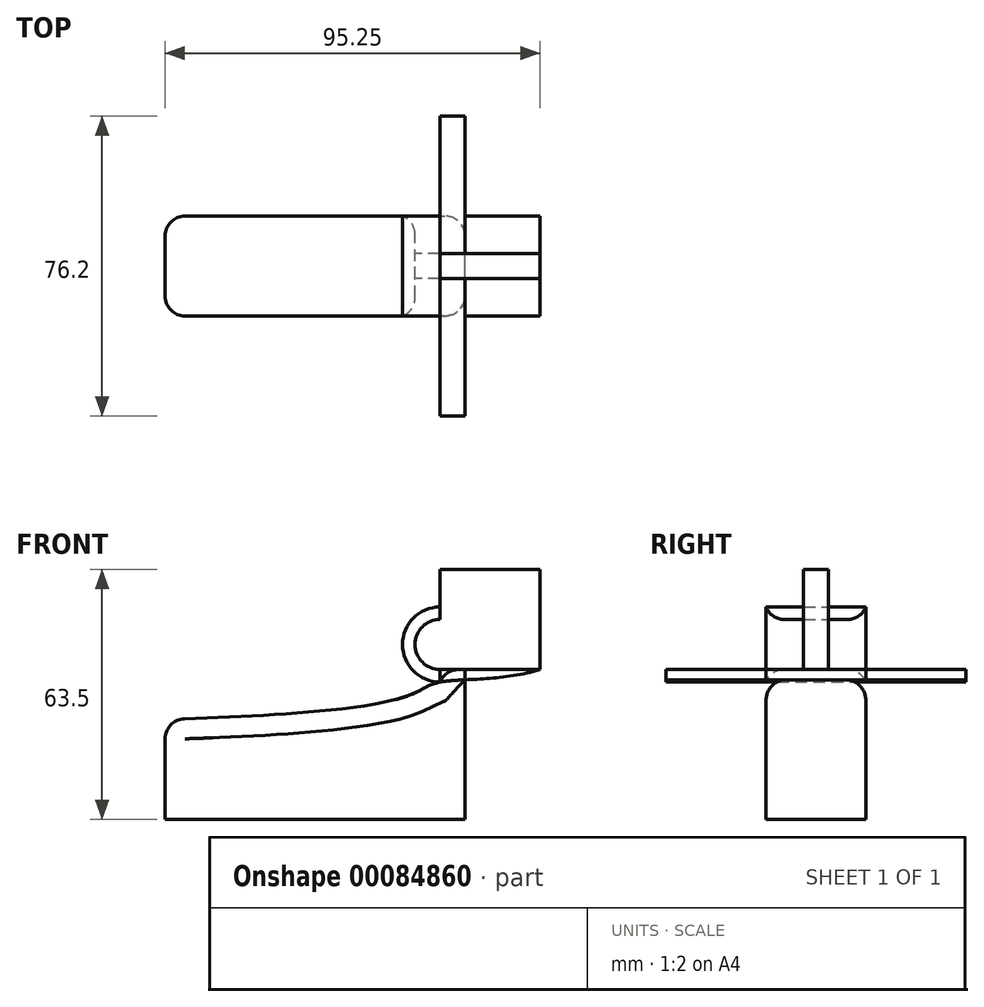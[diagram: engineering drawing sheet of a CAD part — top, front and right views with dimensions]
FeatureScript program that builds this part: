
annotation { "Feature Type Name" : "Feature", "Feature Type Description" : "" }
export const myFeature = defineFeature(function(context is Context, id is Id, definition is map)
    precondition{}
    {
        {
            var Q0;
            Q0=qCreatedBy(makeId("Front.planeOp"),FACE);
            var sketch = newSketch(context, id + "F0", { "sketchPlane" : qUnion([Q0])});
            skLineSegment(sketch, "E0.bottom", {"start": v(-38.1, -12.7) * mm, "end": v(38.1, -12.7) * mm});
            skLineSegment(sketch, "E0.top", {"start": v(-38.1, 12.7) * mm, "end": v(38.1, 12.7) * mm});
            skLineSegment(sketch, "E0.left", {"start": v(-38.1, -12.7) * mm, "end": v(-38.1, 12.7) * mm});
            skLineSegment(sketch, "E0.right", {"start": v(38.1, -12.7) * mm, "end": v(38.1, 12.7) * mm});
            skPoint(sketch, "E0.middle", {"position": v(0, 0) * mm});
            skLineSegment(sketch, "E1.bottom", {"start": v(31.75, 25.4) * mm, "end": v(57.15, 25.4) * mm});
            skLineSegment(sketch, "E1.top", {"start": v(31.75, 50.8) * mm, "end": v(57.15, 50.8) * mm});
            skLineSegment(sketch, "E1.left", {"start": v(31.75, 38.1) * mm, "end": v(31.75, 50.8) * mm});
            skLineSegment(sketch, "E1.right", {"start": v(57.15, 25.4) * mm, "end": v(57.15, 50.8) * mm});
            skPoint(sketch, "E1.middle", {"position": v(44.45, 38.1) * mm});
            skLineSegment(sketch, "E2", {"start": v(38.1, 12.7) * mm, "end": v(38.1, 25.4) * mm});
            skArc(sketch, "E3", {"start": v(31.75, 38.1) * mm, "mid": v(25.4, 31.75) * mm, "end": v(31.75, 25.4) * mm});
            skArc(sketch, "E4.0", {"start": v(31.75, 41.27) * mm, "mid": v(22.22, 31.75) * mm, "end": v(31.75, 22.23) * mm});
            skLineSegment(sketch, "E5", {"start": v(31.75, 22.23) * mm, "end": v(31.75, 25.4) * mm});
            skLineSegment(sketch, "E6", {"start": v(31.75, 41.27) * mm, "end": v(31.75, 38.1) * mm});
            skFitSpline(sketch, "E7", {"points": [v(-38.1, 12.7) * mm, v(31.75, 22.23) * mm, v(57.15, 25.4) * mm], "startDerivative": vector(339.49, 10.11) * mm, "endDerivative": vector(73.4, 23.68) * mm});
            skSolve(sketch);
        }
        {
            var Q0;
            Q0=makeQuery(id+"F0.imprint","IMPRINT",FACE,{"disambiguationData":[TD([[makeQuery(id+"F0.imprint","IMPRINT",EDGE,{"derivedFrom":sQuery(id+"F0.wireOp",EDGE,"E0.bottom")}),1.0]])]});
            var Q1;
            Q1=makeQuery(id+"F0.imprint","IMPRINT",FACE,{"disambiguationData":[TD([[makeQuery(id+"F0.imprint","IMPRINT",EDGE,{"derivedFrom":sQuery(id+"F0.wireOp",EDGE,"E3")}),-1.0]])]});
            var Q2;
            {var subQ1=sQuery(id+"F0.wireOp",EDGE,"E1.bottom");var subQ3=sQuery(id+"F0.wireOp",EDGE,"E2");var subQ4=makeQuery(id+"F0.imprint","INTERSECT",VERTEX,{"derivedFrom":[subQ1,subQ3]});Q2=makeQuery(id+"F0.imprint","IMPRINT",FACE,{"disambiguationData":[TD([[makeQuery(id+"F0.imprint","IMPRINT",EDGE,{"disambiguationData":[TD([[subQ4,1.0]])],"derivedFrom":subQ3}),-1.0]])]});}
            var Q3;
            {var subQ0=sQuery(id+"F0.wireOp",EDGE,"E0.top");Q3=makeQuery(id+"F0.imprint","IMPRINT",FACE,{"disambiguationData":[TD([[makeQuery(id+"F0.imprint","IMPRINT",EDGE,{"derivedFrom":subQ0}),1.0]])]});}
            extrude(context, id + "F1", {"entities" : qUnion([Q0, Q1, Q2, Q3]), "endBound" : BoundingType.SYMMETRIC, "depth" : 25.4 * mm});
        }
        {
            var Q0;
            {var subQ0=sQuery(id+"F0.wireOp",EDGE,"E5");Q0=makeQuery(id+"F0.imprint","IMPRINT",FACE,{"disambiguationData":[TD([[makeQuery(id+"F0.imprint","IMPRINT",EDGE,{"derivedFrom":subQ0}),-1.0]])]});}
            extrude(context, id + "F2", {"entities" : qUnion([Q0]), "endBound" : BoundingType.SYMMETRIC, "depth" : 76.2 * mm});
        }
        {
            var Q0;
            Q0=makeQuery(id+"F0.imprint","IMPRINT",FACE,{"disambiguationData":[TD([[makeQuery(id+"F0.imprint","IMPRINT",EDGE,{"derivedFrom":sQuery(id+"F0.wireOp",EDGE,"E1.top")}),-1.0]])]});
            extrude(context, id + "F3", {"entities" : qUnion([Q0]), "endBound" : BoundingType.SYMMETRIC, "depth" : 6.35 * mm});
        }
        {
            var Q0;
            {var subQ0=sQuery(id+"F0.wireOp",EDGE,"E7");Q0=makeQuery(id+"F1.opExtrude","CAP_EDGE",EDGE,{"disambiguationData":[OSD([subQ0]),TDD([makeQuery(id+"F0.imprint","IMPRINT",EDGE,{"disambiguationData":[TD([[makeQuery(id+"F0.imprint","INTERSECT",VERTEX,{"derivedFrom":[sQuery(id+"F0.wireOp",EDGE,"E0.top"),sQuery(id+"F0.wireOp",EDGE,"E0.left"),subQ0]}),-1.0]])],"derivedFrom":subQ0}),makeQuery(id+"F0.imprint","IMPRINT",EDGE,{"disambiguationData":[TD([[makeQuery(id+"F0.imprint","INTERSECT",VERTEX,{"derivedFrom":[sQuery(id+"F0.wireOp",EDGE,"E2"),subQ0]}),1.0]])],"derivedFrom":subQ0})])],"isStart":false});}
            var Q1;
            {var subQ0=sQuery(id+"F0.wireOp",EDGE,"E7");Q1=makeQuery(id+"F1.opExtrude","CAP_EDGE",EDGE,{"disambiguationData":[OSD([subQ0]),TDD([makeQuery(id+"F0.imprint","IMPRINT",EDGE,{"disambiguationData":[TD([[makeQuery(id+"F0.imprint","INTERSECT",VERTEX,{"derivedFrom":[sQuery(id+"F0.wireOp",EDGE,"E0.top"),sQuery(id+"F0.wireOp",EDGE,"E0.left"),subQ0]}),-1.0]])],"derivedFrom":subQ0}),makeQuery(id+"F0.imprint","IMPRINT",EDGE,{"disambiguationData":[TD([[makeQuery(id+"F0.imprint","INTERSECT",VERTEX,{"derivedFrom":[sQuery(id+"F0.wireOp",EDGE,"E2"),subQ0]}),1.0]])],"derivedFrom":subQ0})])],"isStart":true});}
            var Q2;
            Q2=makeQuery(id+"F1.opExtrude","CAP_EDGE",EDGE,{"disambiguationData":[OSD([sQuery(id+"F0.wireOp",EDGE,"E0.right"),sQuery(id+"F0.wireOp",EDGE,"E2")])],"isStart":false});
            var Q3;
            Q3=makeQuery(id+"F1.opExtrude","SWEPT_EDGE",EDGE,{"disambiguationData":[OSD([sQuery(id+"F0.wireOp",EDGE,"E0.top"),sQuery(id+"F0.wireOp",EDGE,"E0.left"),sQuery(id+"F0.wireOp",EDGE,"E7")])]});
            var Q4;
            Q4=makeQuery(id+"F1.opExtrude","CAP_EDGE",EDGE,{"disambiguationData":[OSD([sQuery(id+"F0.wireOp",EDGE,"E0.left")])],"isStart":true});
            var Q5;
            Q5=makeQuery(id+"F2.opExtrude","SWEPT_EDGE",EDGE,{"disambiguationData":[OSD([sQuery(id+"F0.wireOp",EDGE,"E1.bottom"),sQuery(id+"F0.wireOp",EDGE,"E3"),sQuery(id+"F0.wireOp",EDGE,"E5")])]});
            var Q6;
            Q6=makeQuery(id+"F1.opExtrude","CAP_EDGE",EDGE,{"disambiguationData":[OSD([sQuery(id+"F0.wireOp",EDGE,"E0.left")])],"isStart":false});
            var Q7;
            Q7=makeQuery(id+"F1.opExtrude","CAP_EDGE",EDGE,{"disambiguationData":[OSD([sQuery(id+"F0.wireOp",EDGE,"E3")])],"isStart":true});
            var Q8;
            Q8=makeQuery(id+"F1.opExtrude","CAP_EDGE",EDGE,{"disambiguationData":[OSD([sQuery(id+"F0.wireOp",EDGE,"E3")])],"isStart":false});
            var Q9;
            Q9=makeQuery(id+"F1.opExtrude","CAP_EDGE",EDGE,{"disambiguationData":[OSD([sQuery(id+"F0.wireOp",EDGE,"E0.right"),sQuery(id+"F0.wireOp",EDGE,"E2")])],"isStart":true});
            fillet(context, id + "F4", {"entities" : qUnion([Q0, Q1, Q2, Q3, Q4, Q5, Q6, Q7, Q8, Q9]), "radius" : 5.08 * mm, "tangentPropagation" : true, "allowEdgeOverflow" : false});
        }
    });
